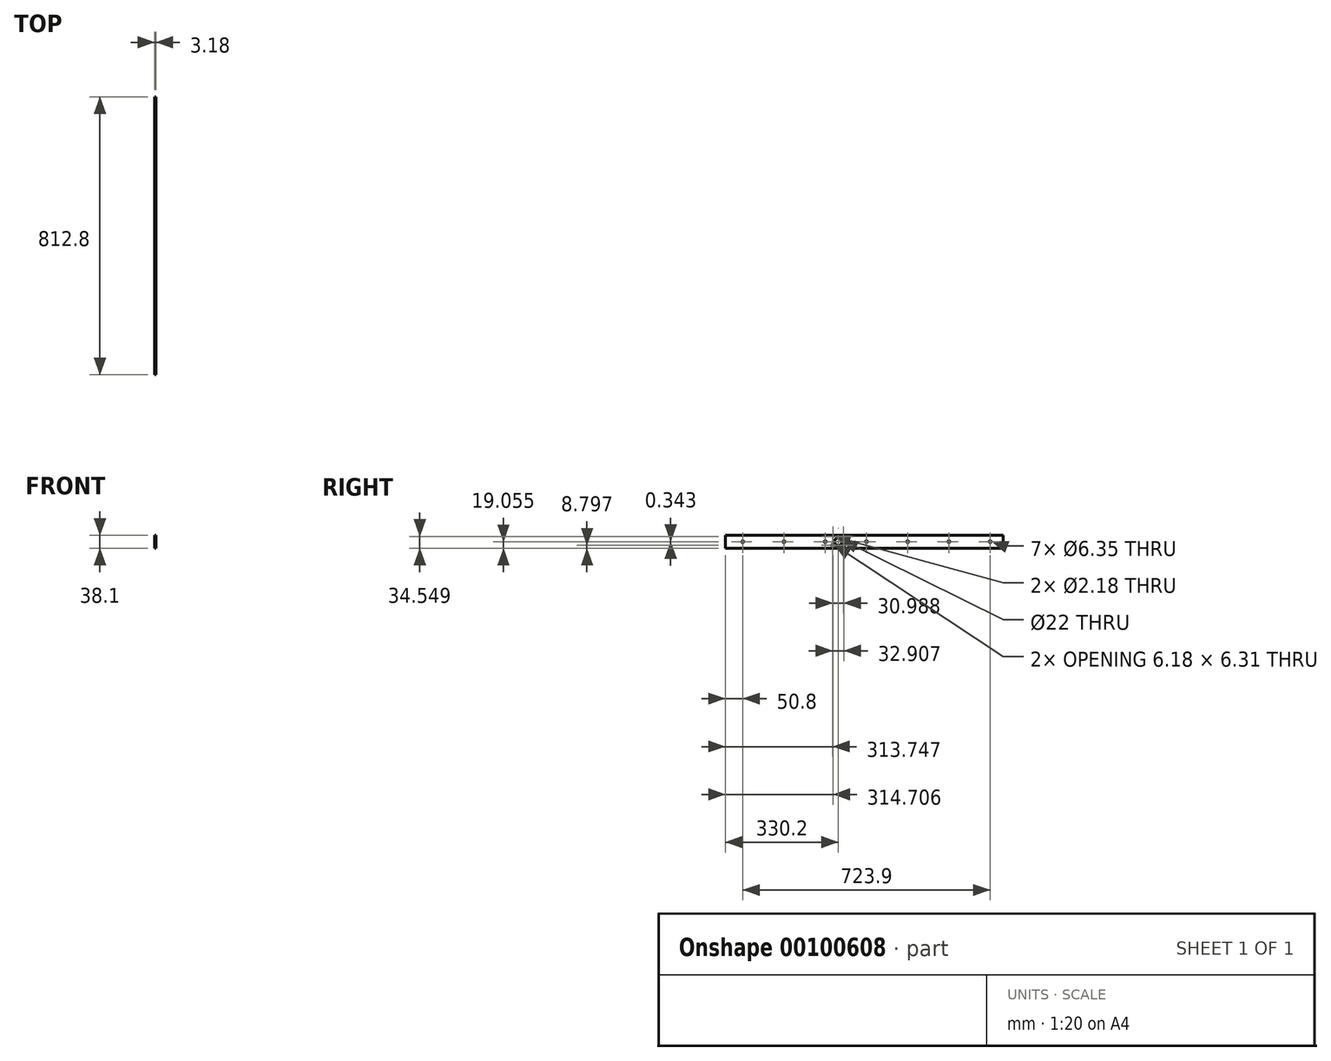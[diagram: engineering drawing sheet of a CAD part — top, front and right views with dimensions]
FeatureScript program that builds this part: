
annotation { "Feature Type Name" : "Feature", "Feature Type Description" : "" }
export const myFeature = defineFeature(function(context is Context, id is Id, definition is map)
    precondition{}
    {
        {
            var Q0;
            Q0=qCreatedBy(makeId("Front.planeOp"),FACE);
            var sketch = newSketch(context, id + "F0", { "sketchPlane" : qUnion([Q0])});
            skLineSegment(sketch, "E0", {"start": v(0, 0) * mm, "end": v(0, 34.92) * mm});
            skLineSegment(sketch, "E1", {"start": v(0, 34.92) * mm, "end": v(-3.18, 34.92) * mm});
            skLineSegment(sketch, "E2", {"start": v(-3.18, 34.92) * mm, "end": v(-3.17, -3.18) * mm});
            skLineSegment(sketch, "E3", {"start": v(-3.17, -3.18) * mm, "end": v(0, -3.18) * mm});
            skLineSegment(sketch, "E4", {"start": v(0, -3.18) * mm, "end": v(0, 0) * mm});
            skLineSegment(sketch, "E5", {"start": v(0, 0) * mm, "end": v(0, 0) * mm});
            skSolve(sketch);
        }
        {
            var Q0;
            Q0=qSketchRegion(id+"F0",true);
            extrude(context, id + "F1", {"entities" : qUnion([Q0]), "depth" : 812.8 * mm});
        }
        {
            var Q0;
            Q0=makeQuery(id+"F1.opExtrude","SWEPT_FACE",FACE,{"disambiguationData":[OSD([sQuery(id+"F0.wireOp",EDGE,"E0")])]});
            var sketch = newSketch(context, id + "F2", { "sketchPlane" : qUnion([Q0])});
            skCircle(sketch, "E6", {"center": v(-482.6, 15.88) * mm, "radius": 11 * mm});
            skPoint(sketch, "E6.centerSnap0", {"position": v(0, 15.88) * mm});
            skCircle(sketch, "E7", {"center": v(-499.11, 5.71) * mm, "radius": 3.18 * mm});
            skLineSegment(sketch, "E8", {"start": v(-508, 34.92) * mm, "end": v(-508, 34.92) * mm});
            skLineSegment(sketch, "E9", {"start": v(-508, 34.92) * mm, "end": v(-457.2, 34.92) * mm, "construction": true});
            skLineSegment(sketch, "E10", {"start": v(-457.2, 34.92) * mm, "end": v(-457.2, 0) * mm, "construction": true});
            skLineSegment(sketch, "E11", {"start": v(-482.6, 34.92) * mm, "end": v(-482.6, 0) * mm, "construction": true});
            skCircle(sketch, "E12.MirrorC", {"center": v(-466.1, 5.72) * mm, "radius": 3.18 * mm});
            skCircle(sketch, "E13", {"center": v(-498.1, 31.37) * mm, "radius": 1.1 * mm});
            skLineSegment(sketch, "E14", {"start": v(-508, 17.46) * mm, "end": v(-457.2, 17.46) * mm, "construction": true});
            skCircle(sketch, "E15.MirrorC", {"center": v(-498.1, 3.56) * mm, "radius": 1.1 * mm});
            skCircle(sketch, "E16.MirrorC", {"center": v(-467.1, 3.56) * mm, "radius": 1.1 * mm});
            skCircle(sketch, "E17.MirrorC", {"center": v(-467.1, 31.37) * mm, "radius": 1.1 * mm});
            skSolve(sketch);
        }
        {
            var Q0;
            Q0=qSketchRegion(id+"F2",true);
            extrude(context, id + "F3", {"entities" : qUnion([Q0]), "operationType" : NewBodyOperationType.REMOVE, "oppositeDirection" : true, "depth" : 25.4 * mm});
        }
        {
            var Q0;
            Q0=makeQuery(id+"F1.opExtrude","SWEPT_FACE",FACE,{"disambiguationData":[OSD([sQuery(id+"F0.wireOp",EDGE,"E2")])]});
            var sketch = newSketch(context, id + "F4", { "sketchPlane" : qUnion([Q0])});
            skCircle(sketch, "E18", {"center": v(762, 15.88) * mm, "radius": 3.18 * mm});
            skPoint(sketch, "E18.centerSnap0", {"position": v(812.8, 15.88) * mm});
            skPoint(sketch, "E19.centerSnap0", {"position": v(0, 15.88) * mm});
            skCircle(sketch, "E20.1.0.0", {"center": v(641.35, 15.93) * mm, "radius": 3.18 * mm});
            skCircle(sketch, "E20.2.0.0", {"center": v(520.7, 15.99) * mm, "radius": 3.18 * mm});
            skCircle(sketch, "E20.3.0.0", {"center": v(400.05, 16.05) * mm, "radius": 3.18 * mm});
            skCircle(sketch, "E20.4.0.0", {"center": v(279.4, 16.1) * mm, "radius": 3.18 * mm});
            skCircle(sketch, "E20.5.0.0", {"center": v(158.75, 16.16) * mm, "radius": 3.18 * mm});
            skLineSegment(sketch, "E20.direction1", {"start": v(762, 15.87) * mm, "end": v(641.35, 15.93) * mm, "construction": true});
            skCircle(sketch, "E21.0.6.0", {"center": v(38.1, 16.22) * mm, "radius": 3.18 * mm});
            skSolve(sketch);
        }
        {
            var Q0;
            Q0 = qSketchRegion(id + "F4", true);
            extrude(context, id + "F5", {"entities" : qUnion([Q0]), "operationType" : NewBodyOperationType.REMOVE, "oppositeDirection" : true, "depth" : 25.4 * mm});
        }
    });
